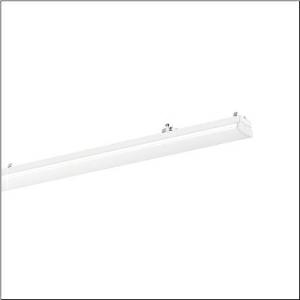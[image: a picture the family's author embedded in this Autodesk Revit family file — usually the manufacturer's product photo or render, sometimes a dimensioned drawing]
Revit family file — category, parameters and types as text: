
# Revit family: licross_r__21_recessed_opal_mo_52tl1ddn46xg_20ca
name_source: partatom
category: Lighting Fixtures
units: mm (PartAtom-declared; Revit-internal decimal feet)

## family parameters
Cut with Voids When Loaded = No
Host = Face
Light Source = No
Part Type = Normal
Room Calculation Point = No
Round Connector Dimension = Use Diameter
Shared = No

## types (1)
- --- (1 x LED, 6320 lm, 36.1 W, 4000K)
    Apparent Load = 36 VA
    CIE Flux Codes = 44 73 91 87 100
    Color Rendering = 80
    Color Temperature = 4000K
    Default Elevation = 1800 mm
    Description = Licross® 21 recessed opal MO, luminaire insert, of sheet steel, galvanised, coil coated, white, length: 1.500mm, width: 66mm, height: 67mm, LED rated luminous flux: 6.320lm, light colour: 840, control gear: DALI 2, with plug, 5-pole, with phase selection, mains connection: 220..240V, AC, 50/60Hz, rated input power: 36W, internal wiring halogen-free, primary optical cover: cover, of PMMA, light emission: direct with ceiling illumination distribution, primary light characteristic: symmetric, protection rating (complete): IP40, insulation class (complete): insulation class I (protective earthing), certification: CE, ENEC, VDE, UKCA, protection symbol: D if used in an environment without relevant dust loads with corresponding accessories, impact resistance: IK06, permissible ambient temperature for indoor applications: -25..+40°C, corresponds to IFS (International Featured Standards) requirements for safety and quality in the food industry, reducing of maximum allowable ambient temperature of 5°C with ceiling mounting, LABS conformity tested according to VDMA 24364:2018-05, packaging unit: 1 piece
    Height = 83 mm
    Lamp = 1 x LED
    Lamp Light Flux = 6320 lm
    Lamp Power = 36.1 W
    Lamp count = 1
    Length = 1500 mm
    Luminous efficacy = 175 lm/W
    Manufacturer = Siteco
    ModVariant = No
    Model = 52TL1DDN46XG
    Mounting Place = Ceiling
    Mounting Type = Pendant
    Number of Poles = 1
    OnlyDefault = Yes
    Power Factor = 1
    Product Name = Licross® 21 recessed opal MO
    Product group = luminaire insert | ceiling pendant
    ProductGroupID = 902
    Protection Class = Protection class I
    Protection Degree = IP 40
    RLX_Detail_Level = 1
    RLX_Emergency_Light_Flux = 0 lm
    RLX_Emergency_Type = 0
    RLX_Emergency_Type_DB = No
    RlxData = <blob elided: 26697 chars, md5=283c587d>
    Socket = socket
    Standby Power = 0 W
    System Light Flux = 6320 lm
    System Power = 36 W
    Type Comments = factory setting: luminous flux: 100 % | dim-lin: 254 | 245 mA
    Type Image = l_1313666.jpg
    URL = http://relux.com
    VarID = @adj_089947
    Voltage = 0 V
    Weight = 0.00 kg
    Width = 76 mm

## geometry (parser evidence)
native form markers: Blend x4, Sweep x13
no freeform markers — native parametric forms only
